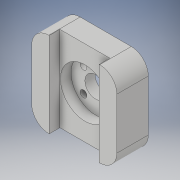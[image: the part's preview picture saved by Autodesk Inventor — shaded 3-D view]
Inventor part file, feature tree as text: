
AUTODESK INVENTOR PART (.ipt)
format: ipt  version: 2018 (Build 220112000, 112)  size: 149,504 bytes
history: native  units: in
note: dims shown in document units (in); Inventor stores cm internally (conversion verified against a paired STEP export)
features: extrude x4, sketch x4, fillet x1
ambient origin geometry x8: Origin, YZ Plane, XZ Plane, XY Plane, X Axis, Y Axis, Z Axis, Center Point
bodies: Solid1 (feature_tree)
feature tree (9):
  extrude  "Extrusion1"  Depth=0.5823in
  extrude  "Extrusion2"  Depth=0.3252in
  extrude  "Extrusion3"  Depth=1.5748in TaperAngle=0.0deg
  extrude  "Extrusion4"  Depth=0.1969in TaperAngle=0.0deg
  fillet  "Fillet1"  Radius=0.3937in
  sketch  "Sketch1"  dims[d0=1.5748in d1=0.5823in]
  sketch  "Sketch2"  dims[d2=0.3252in d3=0.3252in]
  sketch  "Sketch3"  dims[d4=0.1969in d5=1.5748in d6=0.0in]
  sketch  "Sketch4"  dims[d7=0.9055in d8=0.1969in d9=0.0in d10=0.3937in d11=0.1969in d12=0.0in d13=0.2227in d14=0.2227in d15=0.126in d16=1.5748in d18=360.0deg d20=0.1969in d21=0.0in d22=0.315in]
